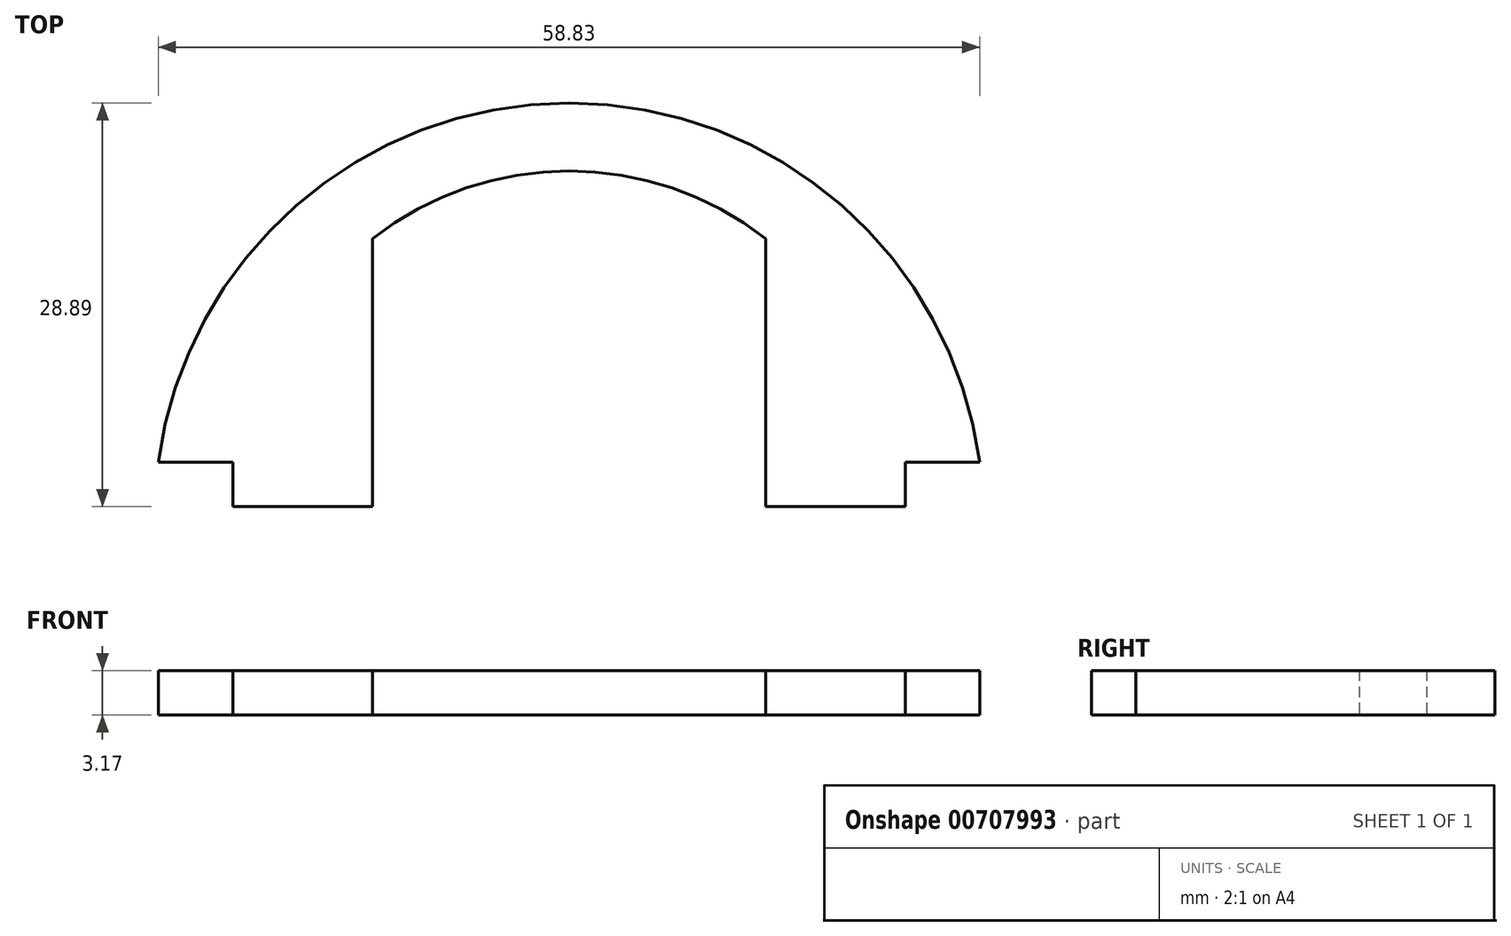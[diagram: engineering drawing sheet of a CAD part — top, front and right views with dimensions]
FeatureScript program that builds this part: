
annotation { "Feature Type Name" : "Feature", "Feature Type Description" : "" }
export const myFeature = defineFeature(function(context is Context, id is Id, definition is map)
    precondition{}
    {
        {
            var Q0;
            Q0=qCreatedBy(makeId("Top.planeOp"), FACE);
            var sketch = newSketch(context, id + "F0", { "sketchPlane" : qUnion([Q0])});
            skPoint(sketch, "E0.0", {"position": v(-29.22, 0.1) * mm});
            skPoint(sketch, "E1.0", {"position": v(29.61, 0.1) * mm});
            skLineSegment(sketch, "E2", {"start": v(-29.22, 0.1) * mm, "end": v(-23.9, 0.1) * mm});
            skArc(sketch, "E3", {"start": v(29.61, 0.1) * mm, "mid": v(0.2, 25.82) * mm, "end": v(-29.22, 0.1) * mm});
            skPoint(sketch, "E4.0", {"position": v(-23.9, 0.1) * mm});
            skPoint(sketch, "E5.0", {"position": v(-13.9, 0.1) * mm});
            skPoint(sketch, "E6.0", {"position": v(24.29, 0.1) * mm});
            skPoint(sketch, "E7.0", {"position": v(14.29, 0.1) * mm});
            skLineSegment(sketch, "E8", {"start": v(-23.9, 0.1) * mm, "end": v(-23.9, -3.07) * mm});
            skLineSegment(sketch, "E9", {"start": v(-23.9, -3.07) * mm, "end": v(-13.9, -3.07) * mm});
            skLineSegment(sketch, "E10", {"start": v(-13.9, -3.07) * mm, "end": v(-13.9, 0.1) * mm});
            skLineSegment(sketch, "E11", {"start": v(-13.9, 0.1) * mm, "end": v(-13.9, 16.1) * mm});
            skLineSegment(sketch, "E12", {"start": v(14.29, 16.1) * mm, "end": v(14.29, 0.1) * mm});
            skLineSegment(sketch, "E13", {"start": v(14.29, 0.1) * mm, "end": v(14.29, -3.07) * mm});
            skLineSegment(sketch, "E14", {"start": v(14.29, -3.07) * mm, "end": v(24.29, -3.07) * mm});
            skLineSegment(sketch, "E15", {"start": v(24.29, -3.07) * mm, "end": v(24.29, 0.1) * mm});
            skLineSegment(sketch, "E16.trimOffspring", {"start": v(24.29, 0.1) * mm, "end": v(29.61, 0.1) * mm});
            skArc(sketch, "E17", {"start": v(14.29, 16.1) * mm, "mid": v(0.2, 20.95) * mm, "end": v(-13.9, 16.1) * mm});
            skSolve(sketch);
        }
        {
            var Q0;
            Q0 = qSketchRegion(id + "F0", true);
            extrude(context, id + "F1", {"entities" : qUnion([Q0]), "depth" : 3.17 * mm, "offsetDistance" : 25 * mm});
        }
    });
